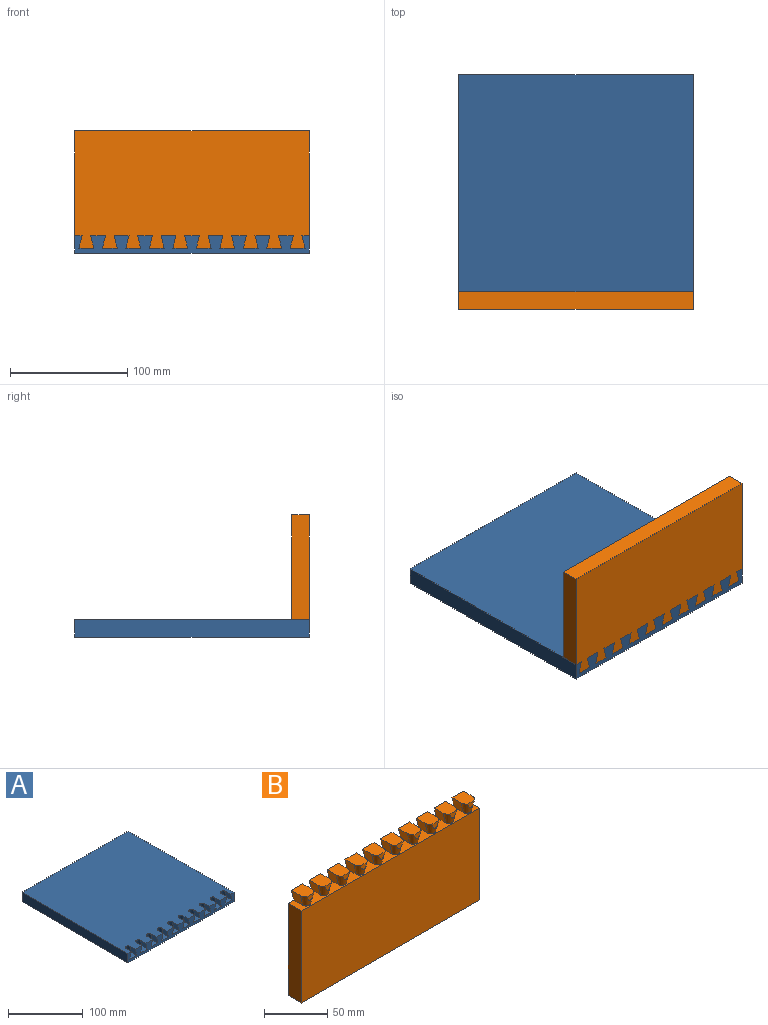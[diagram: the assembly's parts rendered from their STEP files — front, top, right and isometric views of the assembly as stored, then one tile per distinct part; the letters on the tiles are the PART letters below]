
ASSEMBLY  parts=2 mates=1
PART A: 46 faces, bbox 200x200x15 mm
  f0: plane 200x200mm, normal (0,0,1), area 39060.7mm2, adj f1,f2,f4,f5,f6,f7,f9,f10
  f1: plane 200x15mm, normal (0,-1,0), area 1917.1mm2, adj f0,f2,f3,f4,f6,f7,f8,f10
  f2: plane 200x15mm, normal (-1,0,0), area 3000mm2, adj f0,f1,f3,f5
  f3: plane 200x200mm, normal (0,0,-1), area 40000mm2, adj f1,f2,f4,f5
  f4: plane 200x15mm, normal (1,0,0), area 3000mm2, adj f0,f1,f3,f5
  f5: plane 200x15mm, normal (0,1,0), area 3000mm2, adj f0,f2,f3,f4
  f6: plane 10.83x10mm, normal (-0.97,0,-0.24), area 111.6mm2, adj f0,f1,f8,f9
  f7: plane 10.83x10mm, normal (0.97,0,-0.24), area 111.6mm2, adj f0,f1,f8,f9
  f8: plane 16.35x12.7mm, normal (0,0,1), area 190.3mm2, adj f1,f6,f7,f9
  f9: cone r=3.65mm half-angle=14deg, axis (0,0,-1), area 175.3mm2, adj f0,f6,f7,f8
  f10: plane 10.83x10mm, normal (-0.97,0,-0.24), area 111.6mm2, adj f0,f1,f12,f13
  f11: plane 10.83x10mm, normal (0.97,0,-0.24), area 111.6mm2, adj f0,f1,f12,f13
  f12: plane 16.35x12.7mm, normal (0,0,1), area 190.3mm2, adj f1,f10,f11,f13
  f13: cone r=3.65mm half-angle=14deg, axis (0,0,-1), area 175.3mm2, adj f0,f10,f11,f12
  f14: plane 10.83x10mm, normal (-0.97,0,-0.24), area 111.6mm2, adj f0,f1,f16,f17
  f15: plane 10.83x10mm, normal (0.97,0,-0.24), area 111.6mm2, adj f0,f1,f16,f17
  f16: plane 16.35x12.7mm, normal (0,0,1), area 190.3mm2, adj f1,f14,f15,f17
  f17: cone r=3.65mm half-angle=14deg, axis (0,0,-1), area 175.3mm2, adj f0,f14,f15,f16
  f18: plane 10.83x10mm, normal (-0.97,0,-0.24), area 111.6mm2, adj f0,f1,f20,f21
  f19: plane 10.83x10mm, normal (0.97,0,-0.24), area 111.6mm2, adj f0,f1,f20,f21
  f20: plane 16.35x12.7mm, normal (0,0,1), area 190.3mm2, adj f1,f18,f19,f21
  f21: cone r=3.65mm half-angle=14deg, axis (0,0,-1), area 175.3mm2, adj f0,f18,f19,f20
  f22: plane 10.83x10mm, normal (-0.97,0,-0.24), area 111.6mm2, adj f0,f1,f24,f25
  f23: plane 10.83x10mm, normal (0.97,0,-0.24), area 111.6mm2, adj f0,f1,f24,f25
  f24: plane 16.35x12.7mm, normal (0,0,1), area 190.3mm2, adj f1,f22,f23,f25
  f25: cone r=3.65mm half-angle=14deg, axis (0,0,-1), area 175.3mm2, adj f0,f22,f23,f24
  f26: plane 10.83x10mm, normal (-0.97,0,-0.24), area 111.6mm2, adj f0,f1,f28,f29
  f27: plane 10.83x10mm, normal (0.97,0,-0.24), area 111.6mm2, adj f0,f1,f28,f29
  f28: plane 16.35x12.7mm, normal (0,0,1), area 190.3mm2, adj f1,f26,f27,f29
  f29: cone r=3.65mm half-angle=14deg, axis (0,0,-1), area 175.3mm2, adj f0,f26,f27,f28
  f30: plane 10.83x10mm, normal (-0.97,0,-0.24), area 111.6mm2, adj f0,f1,f32,f33
  f31: plane 10.83x10mm, normal (0.97,0,-0.24), area 111.6mm2, adj f0,f1,f32,f33
  f32: plane 16.35x12.7mm, normal (0,0,1), area 190.3mm2, adj f1,f30,f31,f33
  f33: cone r=3.65mm half-angle=14deg, axis (0,0,-1), area 175.3mm2, adj f0,f30,f31,f32
  f34: plane 10.83x10mm, normal (-0.97,0,-0.24), area 111.6mm2, adj f0,f1,f36,f37
  f35: plane 10.83x10mm, normal (0.97,0,-0.24), area 111.6mm2, adj f0,f1,f36,f37
  f36: plane 16.35x12.7mm, normal (0,0,1), area 190.3mm2, adj f1,f34,f35,f37
  f37: cone r=3.65mm half-angle=14deg, axis (0,0,-1), area 175.3mm2, adj f0,f34,f35,f36
  f38: plane 10.83x10mm, normal (-0.97,0,-0.24), area 111.6mm2, adj f0,f1,f40,f41
  f39: plane 10.83x10mm, normal (0.97,0,-0.24), area 111.6mm2, adj f0,f1,f40,f41
  f40: plane 16.35x12.7mm, normal (0,0,1), area 190.3mm2, adj f1,f38,f39,f41
  f41: cone r=3.65mm half-angle=14deg, axis (0,0,-1), area 175.3mm2, adj f0,f38,f39,f40
  f42: plane 16.35x12.7mm, normal (0,0,1), area 190.3mm2, adj f1,f43,f44,f45
  f43: plane 10.83x10mm, normal (-0.97,0,-0.24), area 111.6mm2, adj f0,f1,f42,f44
  f44: cone r=3.65mm half-angle=14deg, axis (0,0,-1), area 175.3mm2, adj f0,f42,f43,f45
  f45: plane 10.83x10mm, normal (0.97,0,-0.24), area 111.6mm2, adj f0,f1,f42,f44
PART B: 56 faces, bbox 200x16.4x100 mm
  f0: plane 7.83x5.42mm, normal (0,-1,0), area 27.6mm2, adj f19,f45
  f1: plane 7.83x5.42mm, normal (0,-1,0), area 27.6mm2, adj f18,f46
  f2: plane 7.83x5.42mm, normal (0,-1,0), area 27.6mm2, adj f17,f47
  f3: plane 7.83x5.42mm, normal (0,-1,0), area 27.6mm2, adj f16,f48
  f4: plane 7.83x5.42mm, normal (0,-1,0), area 27.6mm2, adj f15,f49
  f5: plane 7.83x5.42mm, normal (0,-1,0), area 27.6mm2, adj f14,f50
  f6: plane 7.83x5.42mm, normal (0,-1,0), area 27.6mm2, adj f13,f51
  f7: plane 7.83x5.42mm, normal (0,-1,0), area 27.6mm2, adj f12,f52
  f8: plane 7.83x5.42mm, normal (0,-1,0), area 27.6mm2, adj f11,f53
  f9: plane 7.83x5.42mm, normal (0,-1,0), area 27.6mm2, adj f10,f55
  f10: plane 15x12.7mm, normal (0,0,1), area 183.1mm2, adj f9,f20,f43,f54,f55
  f11: plane 15x12.7mm, normal (0,0,1), area 183.1mm2, adj f8,f20,f41,f42,f53
  f12: plane 15x12.7mm, normal (0,0,1), area 183.1mm2, adj f7,f20,f39,f40,f52
  f13: plane 15x12.7mm, normal (0,0,1), area 183.1mm2, adj f6,f20,f37,f38,f51
  f14: plane 15x12.7mm, normal (0,0,1), area 183.1mm2, adj f5,f20,f35,f36,f50
  f15: plane 15x12.7mm, normal (0,0,1), area 183.1mm2, adj f4,f20,f33,f34,f49
  f16: plane 15x12.7mm, normal (0,0,1), area 183.1mm2, adj f3,f20,f31,f32,f48
  f17: plane 15x12.7mm, normal (0,0,1), area 183.1mm2, adj f2,f20,f29,f30,f47
  f18: plane 15x12.7mm, normal (0,0,1), area 183.1mm2, adj f1,f20,f27,f28,f46
  f19: plane 15x12.7mm, normal (0,0,1), area 183.1mm2, adj f0,f20,f25,f26,f45
  f20: plane 200x100mm, normal (0,1,0), area 18917.1mm2, adj f10,f11,f12,f13,f14,f15,f16,f17
  f21: plane 89.17x15mm, normal (-1,0,0), area 1337.6mm2, adj f20,f22,f24,f44
  f22: plane 200x89.17mm, normal (0,-1,0), area 17834.2mm2, adj f21,f23,f24,f44
  f23: plane 89.17x15mm, normal (1,0,0), area 1337.6mm2, adj f20,f22,f24,f44
  f24: plane 200x15mm, normal (0,0,-1), area 3000mm2, adj f20,f21,f22,f23
  f25: plane 10.83x10mm, normal (0.97,0,-0.24), area 111.6mm2, adj f19,f20,f44,f45
  f26: plane 10.83x10mm, normal (-0.97,0,-0.24), area 111.6mm2, adj f19,f20,f44,f45
  f27: plane 10.83x10mm, normal (0.97,0,-0.24), area 111.6mm2, adj f18,f20,f44,f46
  f28: plane 10.83x10mm, normal (-0.97,0,-0.24), area 111.6mm2, adj f18,f20,f44,f46
  f29: plane 10.83x10mm, normal (0.97,0,-0.24), area 111.6mm2, adj f17,f20,f44,f47
  f30: plane 10.83x10mm, normal (-0.97,0,-0.24), area 111.6mm2, adj f17,f20,f44,f47
  f31: plane 10.83x10mm, normal (0.97,0,-0.24), area 111.6mm2, adj f16,f20,f44,f48
  f32: plane 10.83x10mm, normal (-0.97,0,-0.24), area 111.6mm2, adj f16,f20,f44,f48
  f33: plane 10.83x10mm, normal (0.97,0,-0.24), area 111.6mm2, adj f15,f20,f44,f49
  f34: plane 10.83x10mm, normal (-0.97,0,-0.24), area 111.6mm2, adj f15,f20,f44,f49
  f35: plane 10.83x10mm, normal (0.97,0,-0.24), area 111.6mm2, adj f14,f20,f44,f50
  f36: plane 10.83x10mm, normal (-0.97,0,-0.24), area 111.6mm2, adj f14,f20,f44,f50
  f37: plane 10.83x10mm, normal (0.97,0,-0.24), area 111.6mm2, adj f13,f20,f44,f51
  f38: plane 10.83x10mm, normal (-0.97,0,-0.24), area 111.6mm2, adj f13,f20,f44,f51
  f39: plane 10.83x10mm, normal (0.97,0,-0.24), area 111.6mm2, adj f12,f20,f44,f52
  f40: plane 10.83x10mm, normal (-0.97,0,-0.24), area 111.6mm2, adj f12,f20,f44,f52
  f41: plane 10.83x10mm, normal (0.97,0,-0.24), area 111.6mm2, adj f11,f20,f44,f53
  f42: plane 10.83x10mm, normal (-0.97,0,-0.24), area 111.6mm2, adj f11,f20,f44,f53
  f43: plane 10.83x10mm, normal (-0.97,0,-0.24), area 111.6mm2, adj f10,f20,f44,f55
  f44: plane 200x15mm, normal (0,0,1), area 2060.7mm2, adj f20,f21,f22,f23,f25,f26,f27,f28
  f45: cone r=6.35mm half-angle=14deg, axis (0,0,1), area 145.5mm2, adj f0,f19,f25,f26,f44
  f46: cone r=6.35mm half-angle=14deg, axis (0,0,1), area 145.5mm2, adj f1,f18,f27,f28,f44
  f47: cone r=6.35mm half-angle=14deg, axis (0,0,1), area 145.5mm2, adj f2,f17,f29,f30,f44
  f48: cone r=6.35mm half-angle=14deg, axis (0,0,1), area 145.5mm2, adj f3,f16,f31,f32,f44
  f49: cone r=6.35mm half-angle=14deg, axis (0,0,1), area 145.5mm2, adj f4,f15,f33,f34,f44
  f50: cone r=6.35mm half-angle=14deg, axis (0,0,1), area 145.5mm2, adj f5,f14,f35,f36,f44
  f51: cone r=6.35mm half-angle=14deg, axis (0,0,1), area 145.5mm2, adj f6,f13,f37,f38,f44
  f52: cone r=6.35mm half-angle=14deg, axis (0,0,1), area 145.5mm2, adj f7,f12,f39,f40,f44
  f53: cone r=6.35mm half-angle=14deg, axis (0,0,1), area 145.5mm2, adj f8,f11,f41,f42,f44
  f54: plane 10.83x10mm, normal (0.97,0,-0.24), area 111.6mm2, adj f10,f20,f44,f55
  f55: cone r=6.35mm half-angle=14deg, axis (0,0,1), area 145.5mm2, adj f9,f10,f43,f44,f54
PLACE A at identity fixed
PLACE B rot(axis=(1,0,0),180deg) t=(-10,0,-10.83)mm
MATE fastened A.f44 <-> B.f45  axis (0,0,1) through (10,10,-10.83)mm
